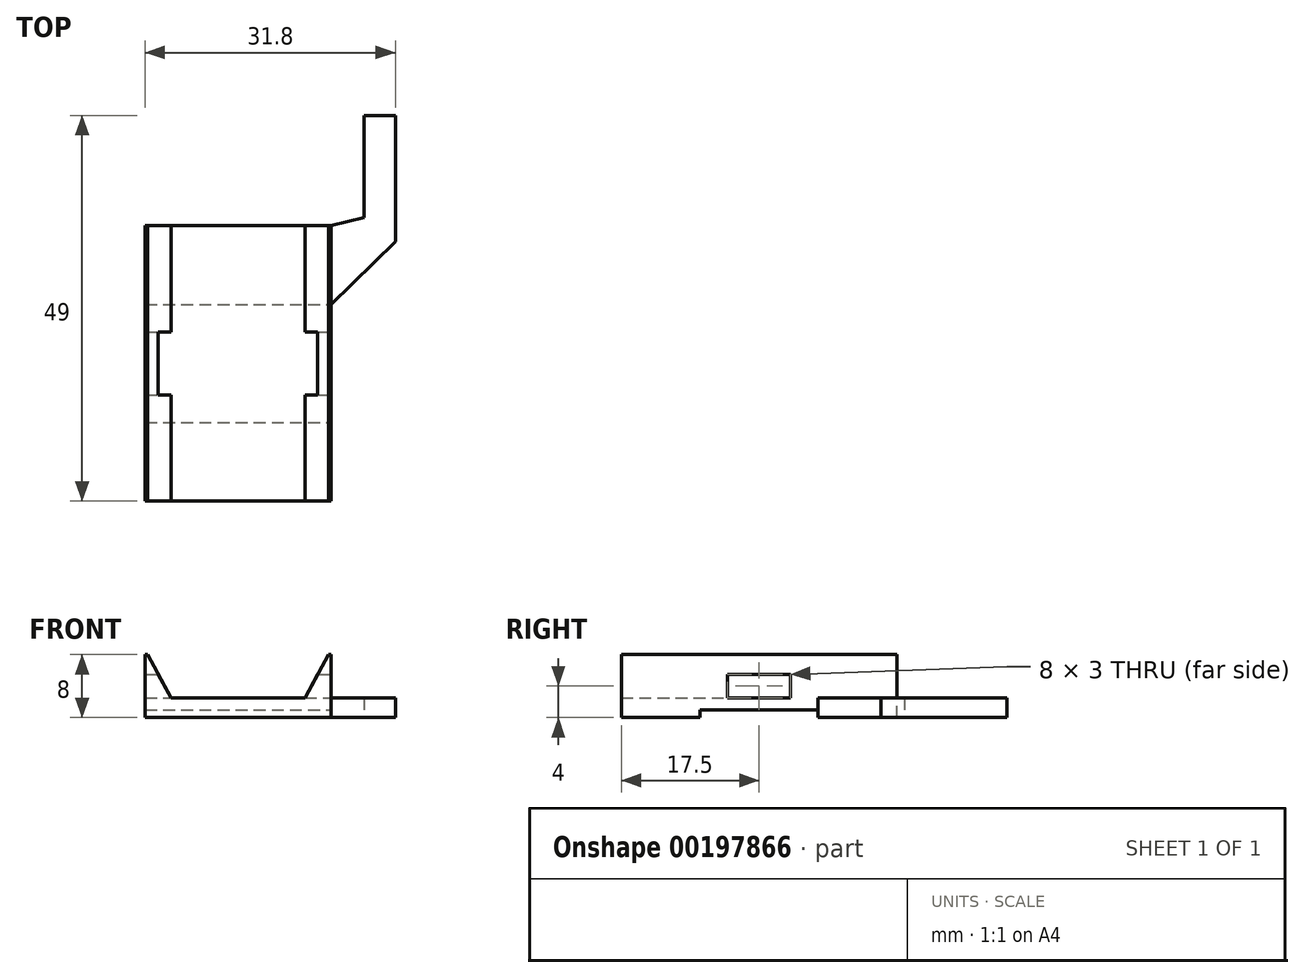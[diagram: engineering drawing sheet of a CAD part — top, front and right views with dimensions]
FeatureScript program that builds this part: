
annotation { "Feature Type Name" : "Feature", "Feature Type Description" : "" }
export const myFeature = defineFeature(function(context is Context, id is Id, definition is map)
    precondition{}
    {
        {
            var Q0;
            Q0=qCreatedBy(makeId("Front.planeOp"),FACE);
            var sketch = newSketch(context, id + "F0", { "sketchPlane" : qUnion([Q0])});
            skLineSegment(sketch, "E0", {"start": v(0, 0) * mm, "end": v(11.8, 0) * mm});
            skLineSegment(sketch, "E1", {"start": v(11.8, 0) * mm, "end": v(11.8, 8) * mm});
            skLineSegment(sketch, "E2", {"start": v(11.8, 8) * mm, "end": v(11.5, 8) * mm});
            skLineSegment(sketch, "E3", {"start": v(11.5, 8) * mm, "end": v(8.5, 2.5) * mm});
            skLineSegment(sketch, "E4", {"start": v(8.5, 2.5) * mm, "end": v(0, 2.5) * mm});
            skLineSegment(sketch, "E5.MirrorCS", {"start": v(0, 0) * mm, "end": v(-11.8, 0) * mm});
            skLineSegment(sketch, "E6.MirrorCS", {"start": v(-11.8, 8) * mm, "end": v(-11.5, 8) * mm});
            skLineSegment(sketch, "E7.MirrorCS", {"start": v(-8.5, 2.5) * mm, "end": v(0, 2.5) * mm});
            skLineSegment(sketch, "E8.MirrorCS", {"start": v(-11.8, 0) * mm, "end": v(-11.8, 8) * mm});
            skLineSegment(sketch, "E9.MirrorCS", {"start": v(-11.5, 8) * mm, "end": v(-8.5, 2.5) * mm});
            skSolve(sketch);
        }
        {
            var Q0;
            Q0 = qSketchRegion(id + "F0", true);
            extrude(context, id + "F1", {"entities" : qUnion([Q0]), "endBound" : BoundingType.SYMMETRIC, "depth" : 35 * mm});
        }
        {
            var Q0;
            Q0=qCreatedBy(makeId("Right.planeOp"),FACE);
            var sketch = newSketch(context, id + "F2", { "sketchPlane" : qUnion([Q0])});
            skLineSegment(sketch, "E10.bottom", {"start": v(4, 2.5) * mm, "end": v(-4, 2.5) * mm});
            skLineSegment(sketch, "E10.top", {"start": v(4, 5.5) * mm, "end": v(-4, 5.5) * mm});
            skLineSegment(sketch, "E10.left", {"start": v(4, 2.5) * mm, "end": v(4, 5.5) * mm});
            skLineSegment(sketch, "E10.right", {"start": v(-4, 2.5) * mm, "end": v(-4, 5.5) * mm});
            skPoint(sketch, "E10.middle", {"position": v(0, 4) * mm});
            skLineSegment(sketch, "E11.bottom", {"start": v(-7.5, 0) * mm, "end": v(7.5, 0) * mm});
            skLineSegment(sketch, "E11.top", {"start": v(-7.5, 1) * mm, "end": v(7.5, 1) * mm});
            skLineSegment(sketch, "E11.left", {"start": v(-7.5, 0) * mm, "end": v(-7.5, 1) * mm});
            skLineSegment(sketch, "E11.right", {"start": v(7.5, 0) * mm, "end": v(7.5, 1) * mm});
            skSolve(sketch);
        }
        {
            var Q0;
            Q0 = qSketchRegion(id + "F2", true);
            extrude(context, id + "F3", {"entities" : qUnion([Q0]), "operationType" : NewBodyOperationType.REMOVE, "endBound" : BoundingType.SYMMETRIC, "oppositeDirection" : true, "depth" : 100 * mm});
        }
        {
            var Q0;
            Q0=qCreatedBy(makeId("Top.planeOp"),FACE);
            var sketch = newSketch(context, id + "F4", { "sketchPlane" : qUnion([Q0])});
            skLineSegment(sketch, "E12", {"start": v(11.8, 17.5) * mm, "end": v(16, 18.5) * mm});
            skLineSegment(sketch, "E13", {"start": v(16, 18.5) * mm, "end": v(16, 31.5) * mm});
            skLineSegment(sketch, "E14", {"start": v(16, 31.5) * mm, "end": v(20, 31.5) * mm});
            skLineSegment(sketch, "E15", {"start": v(20, 31.5) * mm, "end": v(20, 15.5) * mm});
            skLineSegment(sketch, "E16", {"start": v(20, 15.5) * mm, "end": v(11.8, 7.5) * mm});
            skLineSegment(sketch, "E17", {"start": v(11.8, 7.5) * mm, "end": v(11.8, 17.5) * mm});
            skSolve(sketch);
        }
        {
            var Q0;
            Q0 = qSketchRegion(id + "F4", true);
            extrude(context, id + "F5", {"entities" : qUnion([Q0]), "operationType" : NewBodyOperationType.ADD, "depth" : 2.5 * mm});
        }
    });
